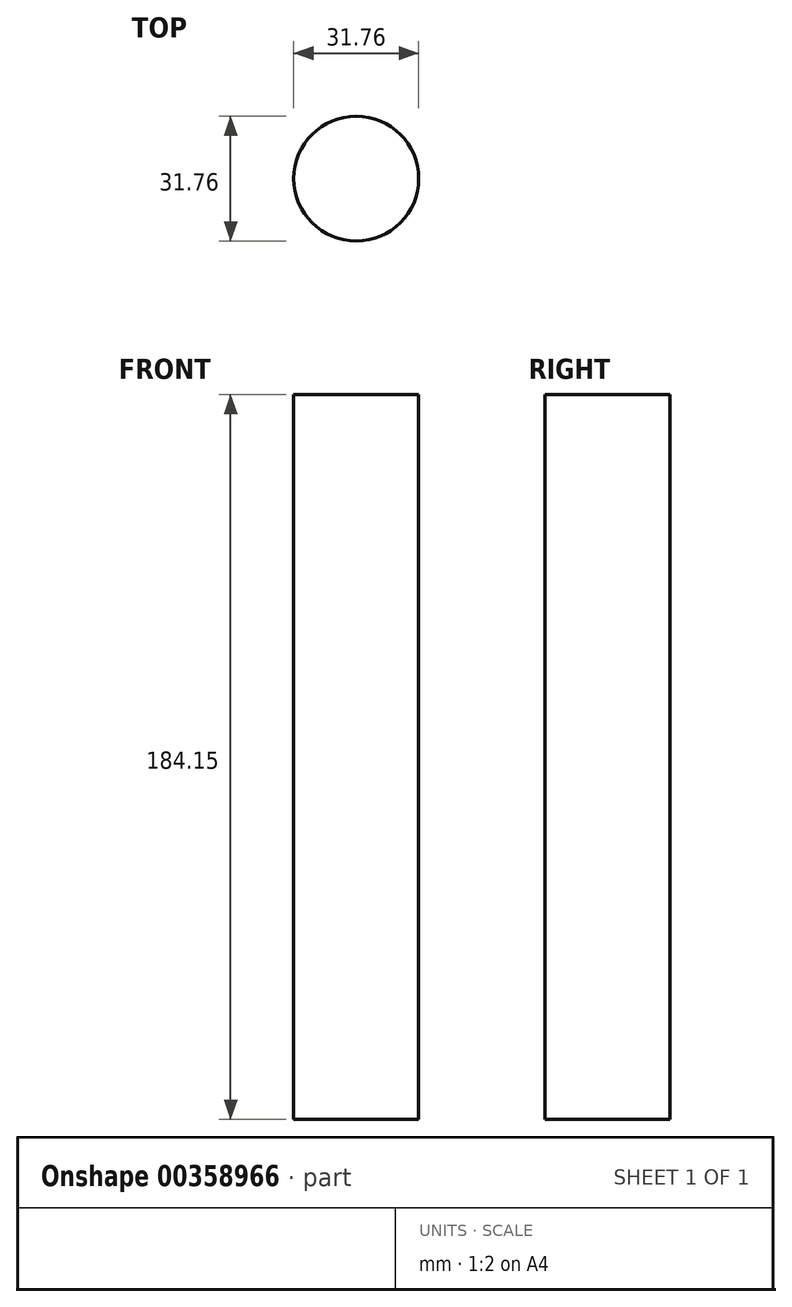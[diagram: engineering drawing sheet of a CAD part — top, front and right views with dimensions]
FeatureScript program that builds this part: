
annotation { "Feature Type Name" : "Feature", "Feature Type Description" : "" }
export const myFeature = defineFeature(function(context is Context, id is Id, definition is map)
    precondition{}
    {
        {
            var Q0;
            Q0=qCreatedBy(makeId("Top.planeOp"),FACE);
            var sketch = newSketch(context, id + "F0", { "sketchPlane" : qUnion([Q0])});
            skCircle(sketch, "E0", {"center": v(0, 0) * mm, "radius": 15.88 * mm});
            skSolve(sketch);
        }
        {
            var Q0;
            Q0 = qSketchRegion(id + "F0", true);
            extrude(context, id + "F1", {"entities" : qUnion([Q0]), "depth" : 184.15 * mm});
        }
    });
